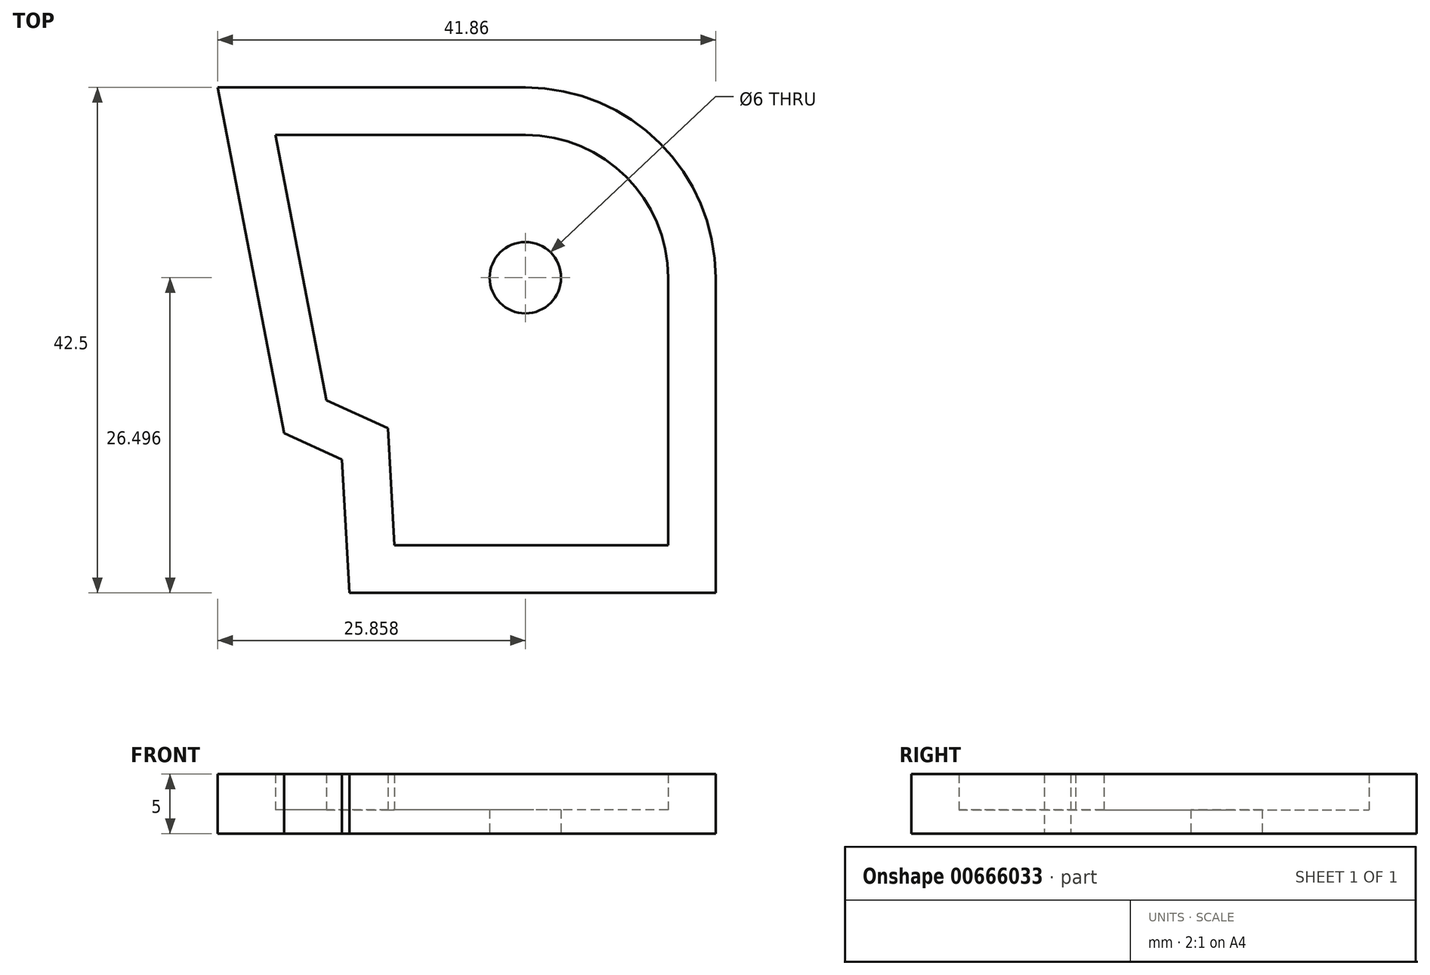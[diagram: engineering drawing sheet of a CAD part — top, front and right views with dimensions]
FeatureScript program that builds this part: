
annotation { "Feature Type Name" : "Feature", "Feature Type Description" : "" }
export const myFeature = defineFeature(function(context is Context, id is Id, definition is map)
    precondition{}
    {
        {
            var Q0;
            Q0=qCreatedBy(makeId("Top.planeOp"),FACE);
            var sketch = newSketch(context, id + "F0", { "sketchPlane" : qUnion([Q0])});
            skCircle(sketch, "E0", {"center": v(-12.03, 21.54) * mm, "radius": 3 * mm});
            skLineSegment(sketch, "E1.0", {"start": v(-32.3, 8.45) * mm, "end": v(-37.9, 37.54) * mm});
            skLineSegment(sketch, "E1.1", {"start": v(-12.03, 37.54) * mm, "end": v(-37.9, 37.54) * mm});
            skLineSegment(sketch, "E1.2", {"start": v(-27.44, 6.23) * mm, "end": v(-26.82, -4.96) * mm});
            skLineSegment(sketch, "E1.3", {"start": v(3.97, -4.96) * mm, "end": v(-26.82, -4.96) * mm});
            skLineSegment(sketch, "E1.4", {"start": v(3.97, -4.96) * mm, "end": v(3.97, 21.54) * mm});
            skLineSegment(sketch, "E1.5", {"start": v(-32.3, 8.45) * mm, "end": v(-27.44, 6.23) * mm});
            skArc(sketch, "E1.6", {"start": v(-12.03, 37.54) * mm, "mid": v(-0.72, 32.85) * mm, "end": v(3.97, 21.54) * mm});
            skLineSegment(sketch, "E2.0", {"start": v(-28.77, 11.24) * mm, "end": v(-23.58, 8.87) * mm});
            skLineSegment(sketch, "E2.1", {"start": v(-23.58, 8.87) * mm, "end": v(-23.03, -0.96) * mm});
            skLineSegment(sketch, "E2.2", {"start": v(-12.03, 33.54) * mm, "end": v(-33.05, 33.54) * mm});
            skArc(sketch, "E2.3", {"start": v(-12.03, 33.54) * mm, "mid": v(-3.55, 30.02) * mm, "end": v(-0.03, 21.54) * mm});
            skLineSegment(sketch, "E2.4", {"start": v(-0.03, -0.96) * mm, "end": v(-0.03, 21.54) * mm});
            skLineSegment(sketch, "E2.5", {"start": v(-28.77, 11.24) * mm, "end": v(-33.05, 33.54) * mm});
            skLineSegment(sketch, "E2.6", {"start": v(-0.03, -0.96) * mm, "end": v(-23.03, -0.96) * mm});
            skSolve(sketch);
        }
        {
            var Q0;
            Q0=makeQuery(id+"F0.imprint","IMPRINT",FACE,{"disambiguationData":[TD([[makeQuery(id+"F0.imprint","IMPRINT",EDGE,{"derivedFrom":sQuery(id+"F0.wireOp",EDGE,"E1.0")}),-1.0]])]});
            var Q1;
            Q1=sQuery(id+"F0.wireOp",EDGE,"E2.5");
            var Q2;
            Q2=sQuery(id+"F0.wireOp",EDGE,"E1.0");
            var Q3;
            Q3=sQuery(id+"F0.wireOp",EDGE,"E1.5");
            var Q4;
            Q4=sQuery(id+"F0.wireOp",EDGE,"E1.2");
            var Q5;
            Q5=sQuery(id+"F0.wireOp",EDGE,"E2.0");
            var Q6;
            Q6=sQuery(id+"F0.wireOp",EDGE,"E2.1");
            var Q7;
            Q7=sQuery(id+"F0.wireOp",EDGE,"E1.4");
            var Q8;
            Q8=sQuery(id+"F0.wireOp",EDGE,"E2.4");
            var Q9;
            Q9=sQuery(id+"F0.wireOp",EDGE,"E2.6");
            var Q10;
            Q10=sQuery(id+"F0.wireOp",EDGE,"E1.3");
            var Q11;
            Q11=sQuery(id+"F0.wireOp",EDGE,"E2.3");
            var Q12;
            Q12=sQuery(id+"F0.wireOp",EDGE,"E1.6");
            var Q13;
            Q13=sQuery(id+"F0.wireOp",EDGE,"E1.1");
            var Q14;
            Q14=sQuery(id+"F0.wireOp",EDGE,"E2.2");
            extrude(context, id + "F1", {"entities" : qUnion([Q0]), "surfaceEntities" : qUnion([Q1, Q2, Q3, Q4, Q5, Q6, Q7, Q8, Q9, Q10, Q11, Q12, Q13, Q14]), "depth" : 5 * mm, "offsetDistance" : 25 * mm});
        }
        {
            var Q0;
            Q0=makeQuery(id+"F0.imprint","IMPRINT",FACE,{"disambiguationData":[TD([[makeQuery(id+"F0.imprint","IMPRINT",EDGE,{"derivedFrom":sQuery(id+"F0.wireOp",EDGE,"E0")}),-1.0]])]});
            extrude(context, id + "F2", {"entities" : qUnion([Q0]), "operationType" : NewBodyOperationType.ADD, "depth" : 2 * mm, "offsetDistance" : 25 * mm});
        }
    });
